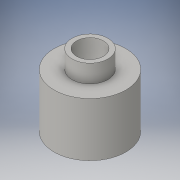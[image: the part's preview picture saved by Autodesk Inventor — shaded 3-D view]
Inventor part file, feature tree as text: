
AUTODESK INVENTOR PART (.ipt)
format: ipt  version: 2016 (Build 200138000, 138)  size: 103,936 bytes
history: native  units: in
note: dims shown in document units (in); Inventor stores cm internally (conversion verified against a paired STEP export)
features: extrude x3, sketch x3
ambient origin geometry x8: Origin, YZ Plane, XZ Plane, XY Plane, X Axis, Y Axis, Z Axis, Center Point
bodies: Solid1 (feature_tree)
feature tree (6):
  extrude  "Extrusion1"  Depth=0.75in TaperAngle=0.0deg
  extrude  "Extrusion2"  Depth=0.25in TaperAngle=0.0deg
  extrude  "Extrusion3"  Depth=1.0in TaperAngle=0.0deg
  sketch  "Sketch1"  dims[d0=1.0in d1=0.75in d2=0.0in]
  sketch  "Sketch2"  dims[d3=0.5in d4=0.25in d5=0.0in]
  sketch  "Sketch3"  dims[d6=0.375in d7=1.0in d8=0.0in]
